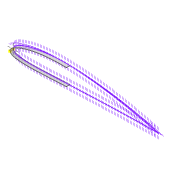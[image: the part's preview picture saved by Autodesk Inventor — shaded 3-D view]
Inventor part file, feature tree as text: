
AUTODESK INVENTOR PART (.ipt)
format: ipt  version: 2022 (Build 260153000, 153)  size: 247,296 bytes
history: native  units: mm
features: sketch x4, extrude x2, shell x1, plane x1
ambient origin geometry x8: Origin, YZ Plane, XZ Plane, XY Plane, X Axis, Y Axis, Z Axis, Center Point
bodies: Solid1 (feature_tree)
feature tree (8):
  extrude  "Extrusion1"  Depth=2.0mm
  shell  "Shell1"  Thickness=5.215mm
  plane  "Work Plane3"
  sketch  "Sketch26"  dims[d69=4.1mm d70=63.6mm]
  sketch  "Sketch34"  dims[d106=200.0mm]
  extrude  "Extrusion16"  Depth=63.6mm
  sketch  "Sketch3"  dims[d0=12.0mm d1=0.0mm d2=2.0mm d68=5.215mm]
  sketch  "Sketch35"  dims[d107=100.0mm d108=0.0mm]
